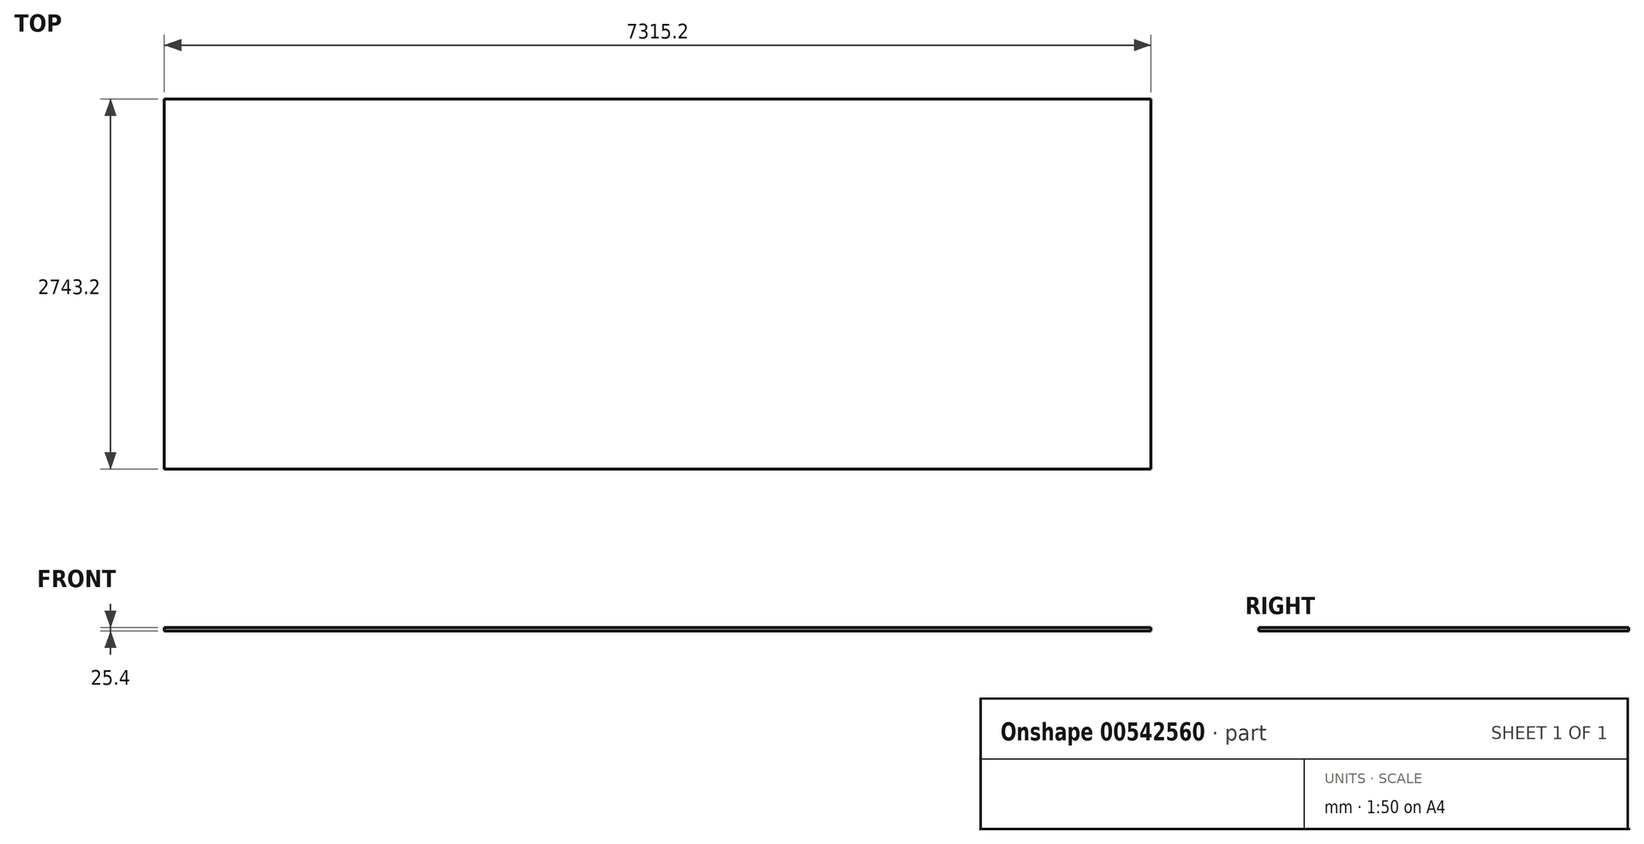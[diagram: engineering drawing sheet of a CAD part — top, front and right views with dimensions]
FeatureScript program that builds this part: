
annotation { "Feature Type Name" : "Feature", "Feature Type Description" : "" }
export const myFeature = defineFeature(function(context is Context, id is Id, definition is map)
    precondition{}
    {
        {
            var Q0;
            Q0=qCreatedBy(makeId("Top.planeOp"),FACE);
            var sketch = newSketch(context, id + "F0", { "sketchPlane" : qUnion([Q0])});
            skLineSegment(sketch, "E0.bottom", {"start": v(3657.6, 1371.6) * mm, "end": v(-3657.6, 1371.6) * mm});
            skLineSegment(sketch, "E0.top", {"start": v(3657.6, -1371.6) * mm, "end": v(-3657.6, -1371.6) * mm});
            skLineSegment(sketch, "E0.left", {"start": v(3657.6, 1371.6) * mm, "end": v(3657.6, -1371.6) * mm});
            skLineSegment(sketch, "E0.right", {"start": v(-3657.6, 1371.6) * mm, "end": v(-3657.6, -1371.6) * mm});
            skPoint(sketch, "E0.middle", {"position": v(0, 0) * mm});
            skSolve(sketch);
        }
        {
            var Q0;
            Q0=qSketchRegion(id+"F0",true);
            extrude(context, id + "F1", {"entities" : qUnion([Q0]), "depth" : 25.4 * mm});
        }
    });
